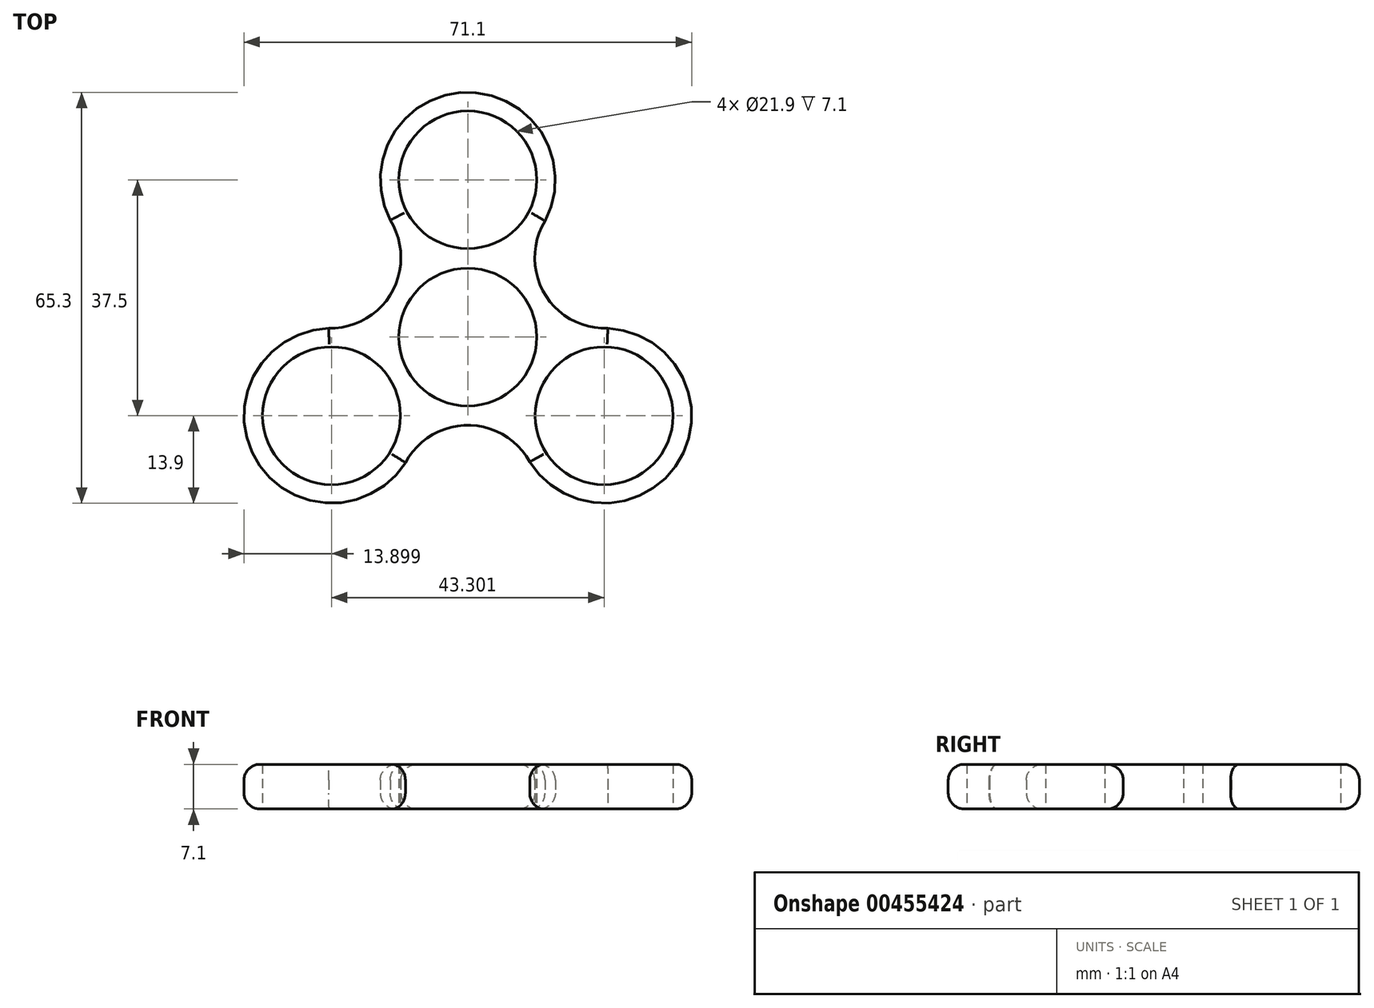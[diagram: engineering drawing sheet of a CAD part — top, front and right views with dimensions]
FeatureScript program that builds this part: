
annotation { "Feature Type Name" : "Feature", "Feature Type Description" : "" }
export const myFeature = defineFeature(function(context is Context, id is Id, definition is map)
    precondition{}
    {
        {
            var Q0;
            Q0=qCreatedBy(makeId("Top.planeOp"),FACE);
            var sketch = newSketch(context, id + "F0", { "sketchPlane" : qUnion([Q0])});
            skCircle(sketch, "E0", {"center": v(0, 0) * mm, "radius": 10.95 * mm});
            skCircle(sketch, "E1", {"center": v(0, 25) * mm, "radius": 10.95 * mm});
            skCircle(sketch, "E2.1.0", {"center": v(-21.65, -12.5) * mm, "radius": 10.95 * mm});
            skCircle(sketch, "E2.2.0", {"center": v(21.65, -12.5) * mm, "radius": 10.95 * mm});
            skArc(sketch, "E3", {"start": v(12.25, 18.44) * mm, "mid": v(12.17, 6.93) * mm, "end": v(22.25, 1.39) * mm});
            skArc(sketch, "E4.1.0", {"start": v(-22.1, 1.4) * mm, "mid": v(-12.09, 7.07) * mm, "end": v(-12.32, 18.57) * mm});
            skArc(sketch, "E4.2.0", {"start": v(9.84, -19.83) * mm, "mid": v(-0.08, -14) * mm, "end": v(-9.92, -19.96) * mm});
            skArc(sketch, "E5.trimOffspring", {"start": v(11.93, 17.86) * mm, "mid": v(-0.07, 38.9) * mm, "end": v(-11.85, 17.74) * mm});
            skArc(sketch, "E6.trimOffspring", {"start": v(9.5, -19.26) * mm, "mid": v(33.72, -19.39) * mm, "end": v(21.29, 1.4) * mm});
            skArc(sketch, "E7.trimOffspring", {"start": v(-21.43, 1.4) * mm, "mid": v(-33.65, -19.51) * mm, "end": v(-9.44, -19.13) * mm});
            skSolve(sketch);
        }
        {
            var Q0;
            Q0=makeQuery(id+"F0.imprint","IMPRINT",FACE,{"disambiguationData":[TD([[makeQuery(id+"F0.imprint","IMPRINT",EDGE,{"derivedFrom":sQuery(id+"F0.wireOp",EDGE,"E0")}),-1.0]])]});
            extrude(context, id + "F1", {"entities" : qUnion([Q0]), "depth" : 7.1 * mm});
        }
        {
            var Q0;
            Q0=makeQuery(id+"F1.opExtrude","CAP_EDGE",EDGE,{"disambiguationData":[OSD([sQuery(id+"F0.wireOp",EDGE,"E7.trimOffspring")])],"isStart":false});
            var Q1;
            Q1=makeQuery(id+"F1.opExtrude","CAP_EDGE",EDGE,{"disambiguationData":[OSD([sQuery(id+"F0.wireOp",EDGE,"E4.1.0")])],"isStart":false});
            var Q2;
            Q2=makeQuery(id+"F1.opExtrude","CAP_EDGE",EDGE,{"disambiguationData":[OSD([sQuery(id+"F0.wireOp",EDGE,"E6.trimOffspring")])],"isStart":false});
            var Q3;
            Q3=makeQuery(id+"F1.opExtrude","CAP_EDGE",EDGE,{"disambiguationData":[OSD([sQuery(id+"F0.wireOp",EDGE,"E4.2.0")])],"isStart":false});
            var Q4;
            Q4=makeQuery(id+"F1.opExtrude","CAP_EDGE",EDGE,{"disambiguationData":[OSD([sQuery(id+"F0.wireOp",EDGE,"E3")])],"isStart":false});
            var Q5;
            Q5=makeQuery(id+"F1.opExtrude","CAP_EDGE",EDGE,{"disambiguationData":[OSD([sQuery(id+"F0.wireOp",EDGE,"E5.trimOffspring")])],"isStart":false});
            fillet(context, id + "F2", {"entities" : qUnion([Q0, Q1, Q2, Q3, Q4, Q5]), "radius" : 2.5 * mm, "tangentPropagation" : true, "rho" : .4, "crossSection" : FilletCrossSection.CONIC, "allowEdgeOverflow" : false});
        }
        {
            var Q0;
            Q0=makeQuery(id+"F1.opExtrude","CAP_EDGE",EDGE,{"disambiguationData":[OSD([sQuery(id+"F0.wireOp",EDGE,"E6.trimOffspring")])],"isStart":true});
            var Q1;
            Q1=makeQuery(id+"F1.opExtrude","CAP_EDGE",EDGE,{"disambiguationData":[OSD([sQuery(id+"F0.wireOp",EDGE,"E4.2.0")])],"isStart":true});
            var Q2;
            Q2=makeQuery(id+"F1.opExtrude","CAP_EDGE",EDGE,{"disambiguationData":[OSD([sQuery(id+"F0.wireOp",EDGE,"E7.trimOffspring")])],"isStart":true});
            var Q3;
            Q3=makeQuery(id+"F1.opExtrude","CAP_EDGE",EDGE,{"disambiguationData":[OSD([sQuery(id+"F0.wireOp",EDGE,"E4.1.0")])],"isStart":true});
            var Q4;
            Q4=makeQuery(id+"F1.opExtrude","CAP_EDGE",EDGE,{"disambiguationData":[OSD([sQuery(id+"F0.wireOp",EDGE,"E5.trimOffspring")])],"isStart":true});
            var Q5;
            Q5=makeQuery(id+"F1.opExtrude","CAP_EDGE",EDGE,{"disambiguationData":[OSD([sQuery(id+"F0.wireOp",EDGE,"E3")])],"isStart":true});
            fillet(context, id + "F3", {"entities" : qUnion([Q0, Q1, Q2, Q3, Q4, Q5]), "radius" : 2.5 * mm, "tangentPropagation" : true, "rho" : .4, "crossSection" : FilletCrossSection.CONIC, "allowEdgeOverflow" : false});
        }
    });
